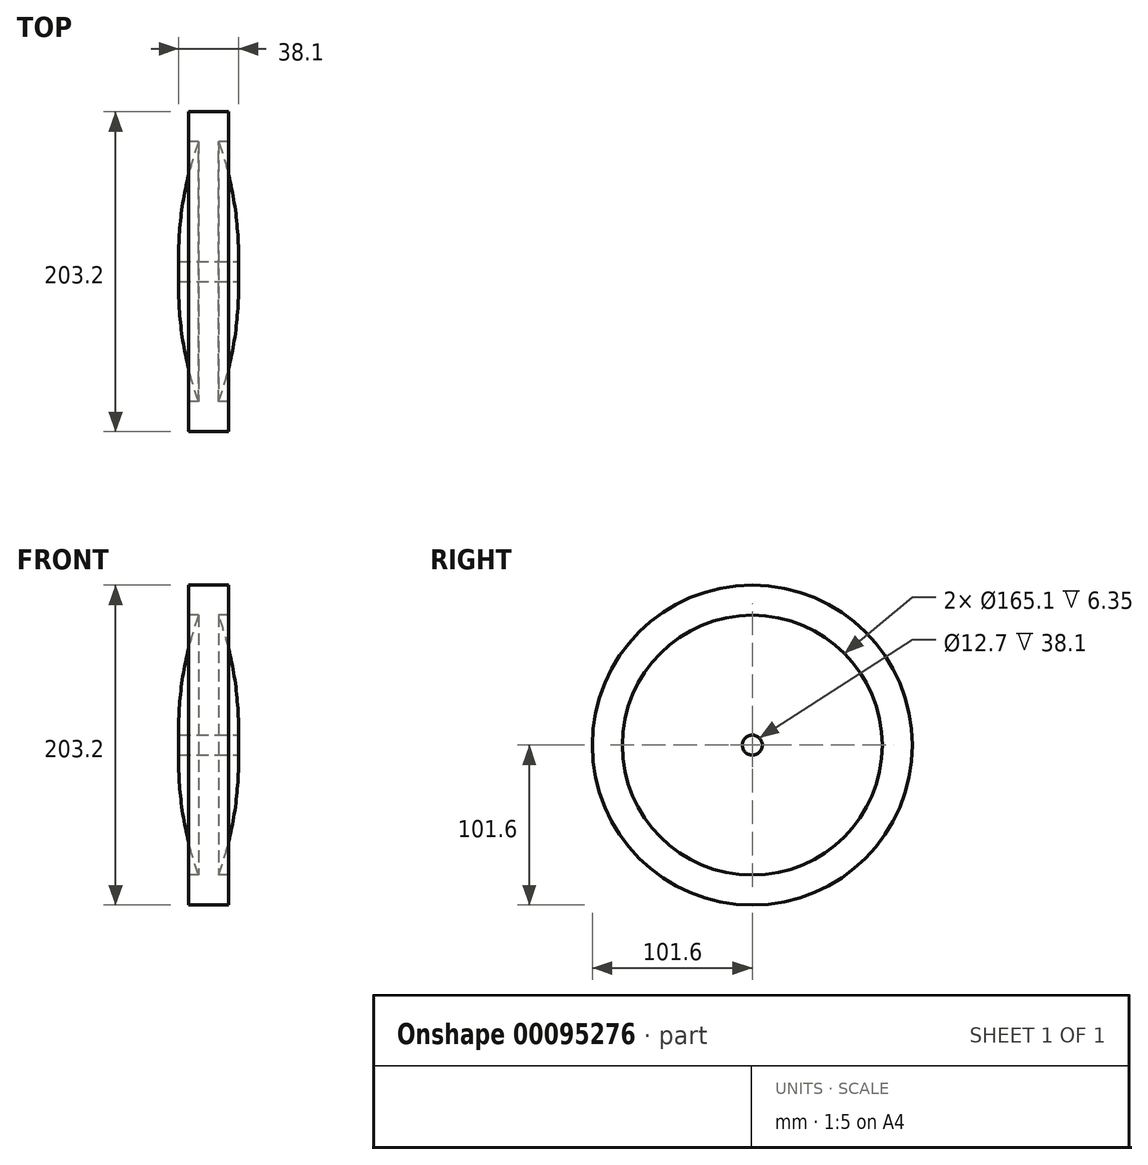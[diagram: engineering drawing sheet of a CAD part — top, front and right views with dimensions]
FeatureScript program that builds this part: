
annotation { "Feature Type Name" : "Feature", "Feature Type Description" : "" }
export const myFeature = defineFeature(function(context is Context, id is Id, definition is map)
    precondition{}
    {
        {
            var Q0;
            Q0=qCreatedBy(makeId("Front.planeOp"),FACE);
            var sketch = newSketch(context, id + "F0", { "sketchPlane" : qUnion([Q0])});
            skLineSegment(sketch, "E0", {"start": v(0, 0) * mm, "end": v(0, 101.6) * mm});
            skLineSegment(sketch, "E1", {"start": v(0, 101.6) * mm, "end": v(12.7, 101.6) * mm});
            skLineSegment(sketch, "E2", {"start": v(12.7, 101.6) * mm, "end": v(12.7, 82.55) * mm});
            skLineSegment(sketch, "E3", {"start": v(12.7, 82.55) * mm, "end": v(6.35, 82.55) * mm});
            skLineSegment(sketch, "E4", {"start": v(0, 0) * mm, "end": v(19.05, 0) * mm});
            skLineSegment(sketch, "E5", {"start": v(19.05, 0) * mm, "end": v(19.05, 9.52) * mm});
            skArc(sketch, "E6", {"start": v(19.05, 9.52) * mm, "mid": v(15.85, 46.59) * mm, "end": v(6.35, 82.55) * mm});
            skLineSegment(sketch, "E7.MirrorCS", {"start": v(0, 101.6) * mm, "end": v(-12.7, 101.6) * mm});
            skLineSegment(sketch, "E8.MirrorCS", {"start": v(-12.7, 101.6) * mm, "end": v(-12.7, 82.55) * mm});
            skLineSegment(sketch, "E9.MirrorCS", {"start": v(-12.7, 82.55) * mm, "end": v(-6.35, 82.55) * mm});
            skLineSegment(sketch, "E10.MirrorCS", {"start": v(-19.05, 0) * mm, "end": v(-19.05, 9.52) * mm});
            skLineSegment(sketch, "E11.MirrorCS", {"start": v(0, 0) * mm, "end": v(-19.05, 0) * mm});
            skArc(sketch, "E12.MirrorCS", {"start": v(-19.05, 9.52) * mm, "mid": v(-15.85, 46.59) * mm, "end": v(-6.35, 82.55) * mm});
            skSolve(sketch);
        }
        {
            var Q0;
            Q0=makeQuery(id+"F0.imprint","IMPRINT",FACE,{"disambiguationData":[TD([[makeQuery(id+"F0.imprint","IMPRINT",EDGE,{"derivedFrom":sQuery(id+"F0.wireOp",EDGE,"E1")}),-1.0]])]});
            var Q1;
            Q1=makeQuery(id+"F0.imprint","IMPRINT",FACE,{"disambiguationData":[TD([[makeQuery(id+"F0.imprint","IMPRINT",EDGE,{"derivedFrom":sQuery(id+"F0.wireOp",EDGE,"E7.MirrorCS")}),1.0]])]});
            var Q2;
            Q2=sQuery(id+"F0.wireOp",EDGE,"E4");
            revolve(context, id + "F1", {"entities" : qUnion([Q0, Q1]), "axis" : qUnion([Q2]), "revolveType" : RevolveType.FULL});
        }
        {
            var Q0;
            Q0=makeQuery(id+"F1.opRevolve","SWEPT_FACE",FACE,{"disambiguationData":[OSD([sQuery(id+"F0.wireOp",EDGE,"E5")])]});
            var sketch = newSketch(context, id + "F2", { "sketchPlane" : qUnion([Q0])});
            skCircle(sketch, "E13", {"center": v(0, 0) * mm, "radius": 6.35 * mm});
            skSolve(sketch);
        }
        {
            var Q0;
            Q0 = qSketchRegion(id + "F2", true);
            extrude(context, id + "F3", {"entities" : qUnion([Q0]), "operationType" : NewBodyOperationType.REMOVE, "endBound" : BoundingType.THROUGH_ALL, "oppositeDirection" : true, "depth" : 25.4 * mm});
        }
    });
